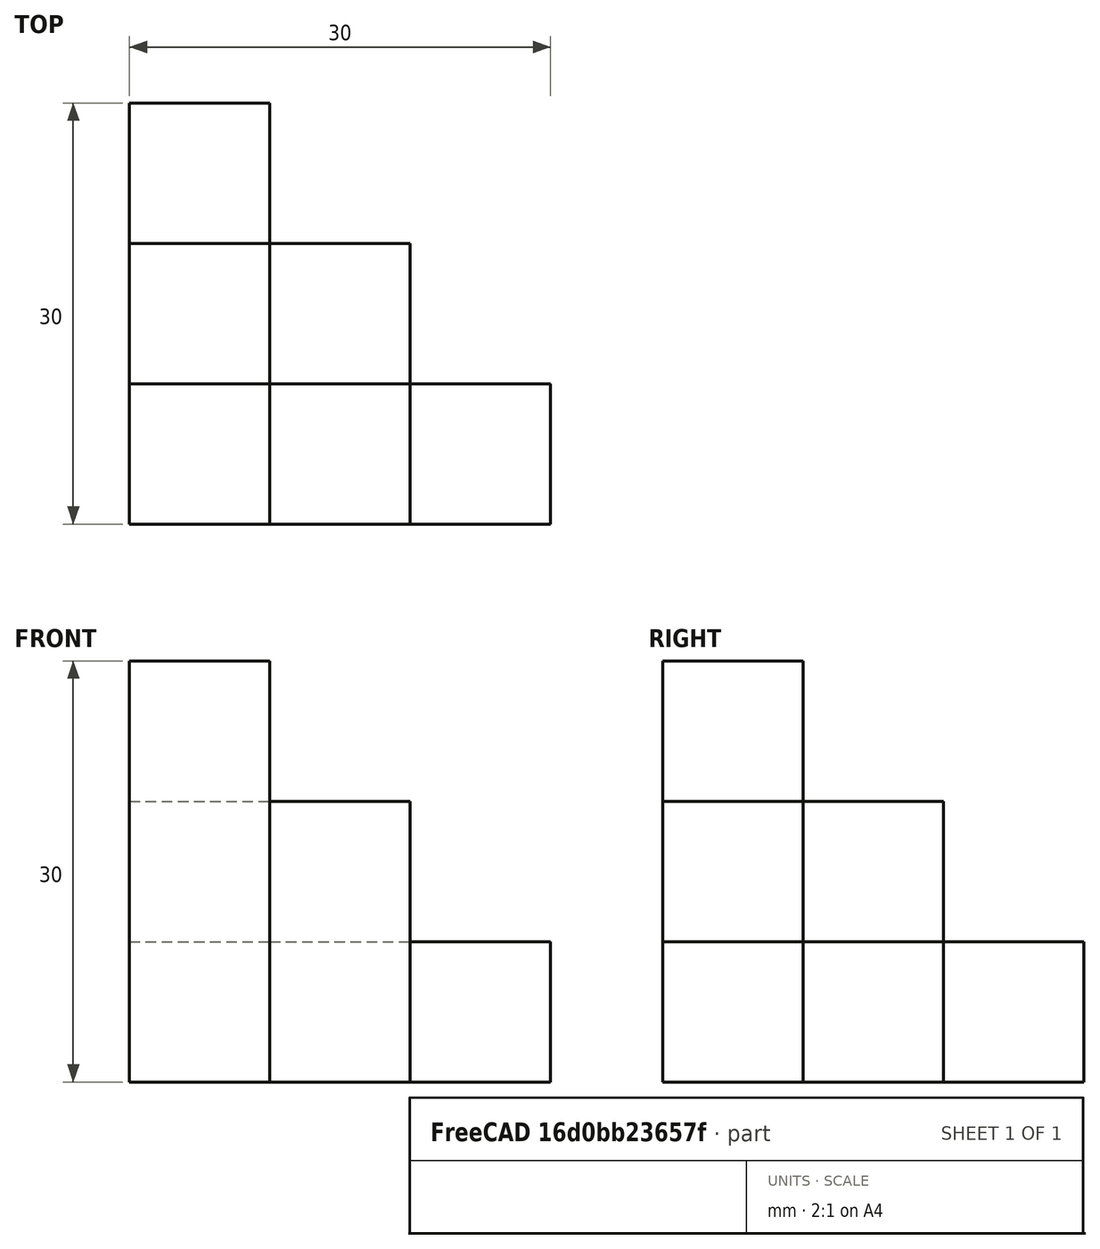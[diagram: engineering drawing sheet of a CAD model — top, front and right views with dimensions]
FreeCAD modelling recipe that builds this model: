
FCSTD DOCUMENT  (FreeCAD 0.21R33694 (Git))
Label: OJT1_T04R01_qubert_3
License: All rights reserved
LicenseURL: http://en.wikipedia.org/wiki/All_rights_reserved
objects: Part::Box×6
note: 6 computed .brp shape members not serialized (recipe doc carries the construction recipe); baked Part::Feature solids carry a one-line shape summary decoded from their .brp

FEATURE [Part::Box] Box  label="Cube"
  AttacherType = Attacher::AttachEngine3D
  Height = 30
  Length = 10
  Width = 10
FEATURE [Part::Box] Box001  label="Cube001"
  AttacherType = Attacher::AttachEngine3D
  Height = 20
  Length = 10
  Placement = pos=(10,0,0) rot=(0,0,1;0rad)
  Width = 10
FEATURE [Part::Box] Box002  label="Cube002"
  AttacherType = Attacher::AttachEngine3D
  Height = 20
  Length = 10
  Placement = pos=(0,10,0) rot=(0,0,1;0rad)
  Width = 10
FEATURE [Part::Box] Box003  label="Cube003"
  AttacherType = Attacher::AttachEngine3D
  Height = 10
  Length = 10
  Placement = pos=(0,20,0) rot=(0,0,1;0rad)
  Width = 10
FEATURE [Part::Box] Box004  label="Cube004"
  AttacherType = Attacher::AttachEngine3D
  Height = 10
  Length = 10
  Placement = pos=(20,0,0) rot=(0,0,1;0rad)
  Width = 10
FEATURE [Part::Box] Box005  label="Cube005"
  AttacherType = Attacher::AttachEngine3D
  Height = 10
  Length = 10
  Placement = pos=(10,10,0) rot=(0,0,1;0rad)
  Width = 10
